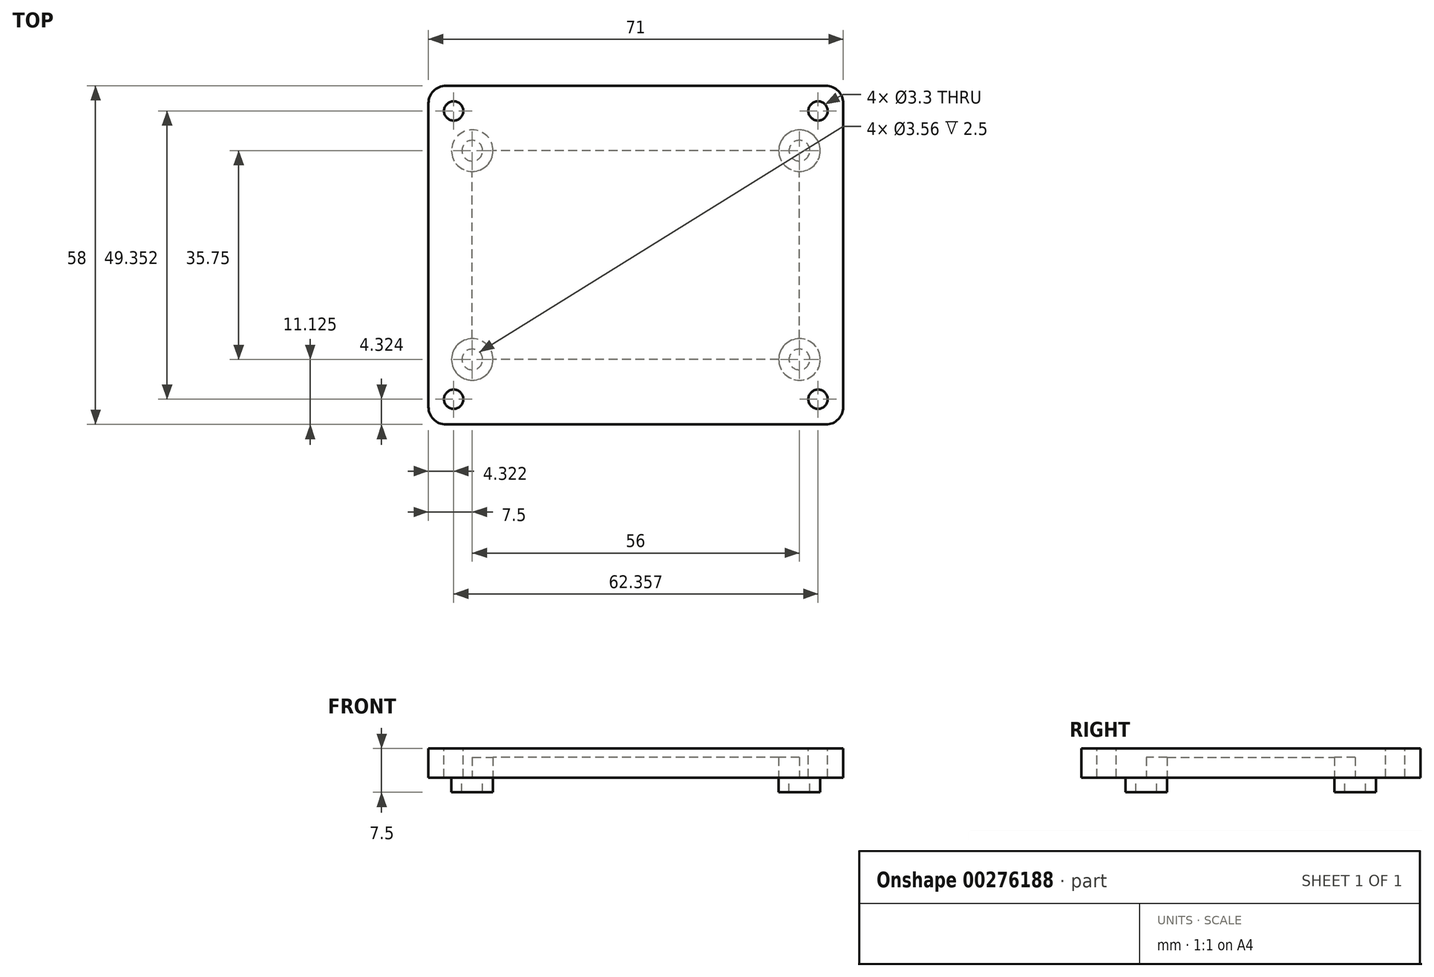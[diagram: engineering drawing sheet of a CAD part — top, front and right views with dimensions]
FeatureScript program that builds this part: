
annotation { "Feature Type Name" : "Feature", "Feature Type Description" : "" }
export const myFeature = defineFeature(function(context is Context, id is Id, definition is map)
    precondition{}
    {
        {
            var Q0;
            Q0=qCreatedBy(makeId("Top.planeOp"),FACE);
            var sketch = newSketch(context, id + "F0", { "sketchPlane" : qUnion([Q0])});
            skLineSegment(sketch, "E0.bottom", {"start": v(-35.5, 29) * mm, "end": v(35.5, 29) * mm});
            skLineSegment(sketch, "E0.top", {"start": v(-35.5, -29) * mm, "end": v(35.5, -29) * mm});
            skLineSegment(sketch, "E0.left", {"start": v(-35.5, 29) * mm, "end": v(-35.5, -29) * mm});
            skLineSegment(sketch, "E0.right", {"start": v(35.5, 29) * mm, "end": v(35.5, -29) * mm});
            skPoint(sketch, "E0.middle", {"position": v(0, 0) * mm});
            skSolve(sketch);
        }
        {
            var Q0;
            Q0=qSketchRegion(id+"F0",true);
            var Q1;
            Q1=qSketchRegion(id+"F5",true);
            extrude(context, id + "F1", {"entities" : qUnion([Q0, Q1]), "depth" : 1.5 * mm + 3.5 * mm});
        }
        {
            var Q0;
            Q0=makeQuery(id+"F1.opExtrude","SWEPT_EDGE",EDGE,{"disambiguationData":[OSD([sQuery(id+"F0.wireOp",EDGE,"E0.bottom"),sQuery(id+"F0.wireOp",EDGE,"E0.left")])]});
            var Q1;
            Q1=makeQuery(id+"F1.opExtrude","SWEPT_EDGE",EDGE,{"disambiguationData":[OSD([sQuery(id+"F0.wireOp",EDGE,"E0.bottom"),sQuery(id+"F0.wireOp",EDGE,"E0.right")])]});
            var Q2;
            Q2=makeQuery(id+"F1.opExtrude","SWEPT_EDGE",EDGE,{"disambiguationData":[OSD([sQuery(id+"F0.wireOp",EDGE,"E0.top"),sQuery(id+"F0.wireOp",EDGE,"E0.right")])]});
            var Q3;
            Q3=makeQuery(id+"F1.opExtrude","SWEPT_EDGE",EDGE,{"disambiguationData":[OSD([sQuery(id+"F0.wireOp",EDGE,"E0.top"),sQuery(id+"F0.wireOp",EDGE,"E0.left")])]});
            fillet(context, id + "F2", {"entities" : qUnion([Q0, Q1, Q2, Q3]), "radius" : 3 * mm, "tangentPropagation" : true, "allowEdgeOverflow" : false});
        }
        {
            var Q0;
            Q0=makeQuery(id+"F1.opExtrude","CAP_FACE",FACE,{"disambiguationData":[OSD([sQuery(id+"F0.wireOp",EDGE,"E0.bottom"),sQuery(id+"F0.wireOp",EDGE,"E0.top"),sQuery(id+"F0.wireOp",EDGE,"E0.left"),sQuery(id+"F0.wireOp",EDGE,"E0.right")])],"isStart":false});
            var sketch = newSketch(context, id + "F3", { "sketchPlane" : qUnion([Q0])});
            skLineSegment(sketch, "E1.bottom", {"start": v(31.18, 24.68) * mm, "end": v(-31.18, 24.68) * mm, "construction": true});
            skLineSegment(sketch, "E1.top", {"start": v(31.18, -24.68) * mm, "end": v(-31.18, -24.68) * mm, "construction": true});
            skLineSegment(sketch, "E1.left", {"start": v(31.18, 24.68) * mm, "end": v(31.18, -24.68) * mm, "construction": true});
            skLineSegment(sketch, "E1.right", {"start": v(-31.18, 24.68) * mm, "end": v(-31.18, -24.68) * mm, "construction": true});
            skPoint(sketch, "E1.middle", {"position": v(0, 0) * mm});
            skCircle(sketch, "E2", {"center": v(-31.18, 24.68) * mm, "radius": 1.65 * mm});
            skCircle(sketch, "E3", {"center": v(-31.18, -24.68) * mm, "radius": 1.65 * mm});
            skCircle(sketch, "E4", {"center": v(31.18, -24.68) * mm, "radius": 1.65 * mm});
            skCircle(sketch, "E5", {"center": v(31.18, 24.68) * mm, "radius": 1.65 * mm});
            skSolve(sketch);
        }
        {
            var Q0;
            Q0=qSketchRegion(id+"F3",true);
            extrude(context, id + "F4", {"entities" : qUnion([Q0]), "operationType" : NewBodyOperationType.REMOVE, "endBound" : BoundingType.THROUGH_ALL, "oppositeDirection" : true, "depth" : 25.4 * mm});
        }
        {
            var Q0;
            Q0=makeQuery(id+"F1.opExtrude","CAP_FACE",FACE,{"disambiguationData":[OSD([sQuery(id+"F0.wireOp",EDGE,"E0.bottom"),sQuery(id+"F0.wireOp",EDGE,"E0.top"),sQuery(id+"F0.wireOp",EDGE,"E0.left"),sQuery(id+"F0.wireOp",EDGE,"E0.right")])],"isStart":true});
            var sketch = newSketch(context, id + "F5", { "sketchPlane" : qUnion([Q0])});
            skLineSegment(sketch, "E6.bottom", {"start": v(28, 17.88) * mm, "end": v(-28, 17.88) * mm, "construction": true});
            skLineSegment(sketch, "E6.top", {"start": v(28, -17.87) * mm, "end": v(-28, -17.87) * mm, "construction": true});
            skLineSegment(sketch, "E6.left", {"start": v(28, 17.88) * mm, "end": v(28, -17.87) * mm, "construction": true});
            skLineSegment(sketch, "E6.right", {"start": v(-28, 17.88) * mm, "end": v(-28, -17.87) * mm, "construction": true});
            skPoint(sketch, "E6.middle", {"position": v(0, 0) * mm});
            skCircle(sketch, "E7", {"center": v(-28, 17.88) * mm, "radius": 3.56 * mm});
            skCircle(sketch, "E8", {"center": v(28, 17.88) * mm, "radius": 3.56 * mm});
            skCircle(sketch, "E9", {"center": v(28, -17.87) * mm, "radius": 3.56 * mm});
            skCircle(sketch, "E10", {"center": v(-28, -17.87) * mm, "radius": 3.56 * mm});
            skCircle(sketch, "E11", {"center": v(-28, 17.88) * mm, "radius": 1.78 * mm});
            skCircle(sketch, "E12", {"center": v(28, 17.88) * mm, "radius": 1.78 * mm});
            skCircle(sketch, "E13", {"center": v(28, -17.87) * mm, "radius": 1.78 * mm});
            skCircle(sketch, "E14", {"center": v(-28, -17.87) * mm, "radius": 1.78 * mm});
            skSolve(sketch);
        }
        {
            var Q0;
            Q0=qSketchRegion(id+"F5",true);
            extrude(context, id + "F6", {"entities" : qUnion([Q0]), "operationType" : NewBodyOperationType.ADD, "depth" : 2.5 * mm});
        }
        {
            var Q0;
            {var subQ0=sQuery(id+"F0.wireOp",EDGE,"E0.left");var subQ1=sQuery(id+"F0.wireOp",EDGE,"E0.bottom");var subQ2=sQuery(id+"F0.wireOp",EDGE,"E0.right");var subQ3=sQuery(id+"F0.wireOp",EDGE,"E0.top");Q0=makeQuery(id+"F6.boolean.opBoolean","SPLIT",FACE,{"disambiguationData":[TD([makeQuery(id+"F1.opExtrude","SWEPT_FACE",FACE,{"disambiguationData":[OSD([subQ1])]})])],"derivedFrom":makeQuery(id+"F1.opExtrude","CAP_FACE",FACE,{"disambiguationData":[OSD([subQ1,subQ3,subQ0,subQ2])],"isStart":true})});}
            var sketch = newSketch(context, id + "F7", { "sketchPlane" : qUnion([Q0])});
            skLineSegment(sketch, "E15.bottom", {"start": v(24.44, 17.88) * mm, "end": v(-24.44, 17.88) * mm});
            skLineSegment(sketch, "E15.top", {"start": v(24.44, -17.88) * mm, "end": v(-24.44, -17.88) * mm});
            skLineSegment(sketch, "E15.left", {"start": v(28, 14.32) * mm, "end": v(28, -14.32) * mm});
            skLineSegment(sketch, "E15.right", {"start": v(-28, 14.32) * mm, "end": v(-28, -14.32) * mm});
            skPoint(sketch, "E15.middle", {"position": v(0, 0) * mm});
            skArc(sketch, "E16.0", {"start": v(-28, 14.32) * mm, "mid": v(-25.49, 15.36) * mm, "end": v(-24.44, 17.88) * mm});
            skArc(sketch, "E17.0", {"start": v(-24.44, -17.88) * mm, "mid": v(-25.49, -15.36) * mm, "end": v(-28, -14.32) * mm});
            skArc(sketch, "E18.0", {"start": v(28, -14.32) * mm, "mid": v(25.49, -15.36) * mm, "end": v(24.44, -17.88) * mm});
            skArc(sketch, "E19.0", {"start": v(24.44, 17.88) * mm, "mid": v(25.49, 15.36) * mm, "end": v(28, 14.32) * mm});
            skPoint(sketch, "E20.orphan", {"position": v(28, -17.88) * mm});
            skPoint(sketch, "E21.orphan", {"position": v(-28, -17.88) * mm});
            skSolve(sketch);
        }
        {
            var Q0;
            Q0=qSketchRegion(id+"F7",true);
            extrude(context, id + "F8", {"entities" : qUnion([Q0]), "operationType" : NewBodyOperationType.REMOVE, "oppositeDirection" : true, "depth" : 3.5 * mm});
        }
    });
